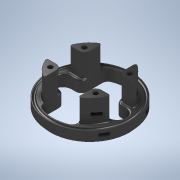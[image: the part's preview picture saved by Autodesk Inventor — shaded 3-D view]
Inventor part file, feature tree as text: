
AUTODESK INVENTOR PART (.ipt)
format: ipt  version: 2020 (Build 240168000, 168)  size: 555,520 bytes
history: native  units: in
note: dims shown in document units (in); Inventor stores cm internally (conversion verified against a paired STEP export)
features: sketch x8, extrude x4, mirror x4, revolve x2, hole x2, fillet x2
ambient origin geometry x8: Origin, YZ Plane, XZ Plane, XY Plane, X Axis, Y Axis, Z Axis, Center Point
bodies: Solid1 (feature_tree)
feature tree (22):
  revolve  "Revolution1"  Angle=90.0deg
  extrude  "Extrusion1"  Depth=1.5in
  revolve  "Revolution2"  [1 undecoded]
  hole  "Hole1"  [1 undecoded]
  extrude  "Extrusion2"  Depth=0.125in
  extrude  "Extrusion3"  TaperAngle=90.0deg  [1 undecoded]
  mirror  "Mirror1"
  mirror  "Mirror2"
  hole  "Hole3"  [1 undecoded]
  extrude  "Extrusion7"  Depth=1.0in TaperAngle=0.0deg
  mirror  "Mirror7"
  mirror  "Mirror8"
  fillet  "Fillet2"  Radius=0.5in
  fillet  "Fillet3"  Radius=0.385in
  sketch  "Sketch1"  dims[d0=1.74in d3=90.0deg]
  sketch  "Sketch2"  dims[d4=1.5in d7=1.5in]
  sketch  "Sketch3"  dims[d8=0.1in d9=0.75in]
  sketch  "Sketch4"  dims[d10=2.4in d11=1.5in]
  sketch  "Sketch5"  dims[d12=0.0in d13=0.0in d14=0.125in]
  sketch  "Sketch6"  dims[d15=1.75in d16=90.0deg]
  sketch  "Sketch12"  dims[d17=0.125in d19=2.5in]
  sketch  "Sketch13"  dims[d20=1.5in d21=0.205in d22=0.75in d23=0.375in d24=0.25in d25=0.5635in d26=0.375in d27=0.0in d28=1.0in d29=0.0in d30=0.5in d31=0.385in d32=0.1875in d33=0.0in d54=1.0in d55=1.5in d56=2.0in d57=0.205in d58=0.75in d59=0.375in d60=0.25in d61=0.5635in d62=0.75in d63=0.0in d64=0.385in d65=0.1875in d66=0.0in d67=0.25in d68=0.0625in d69=1.85in]
note: 4 required parameter values undecoded (feature->parameter linkage not recoverable at this tier; creation-order binding heuristic only, values carry confidence <= 0.55)